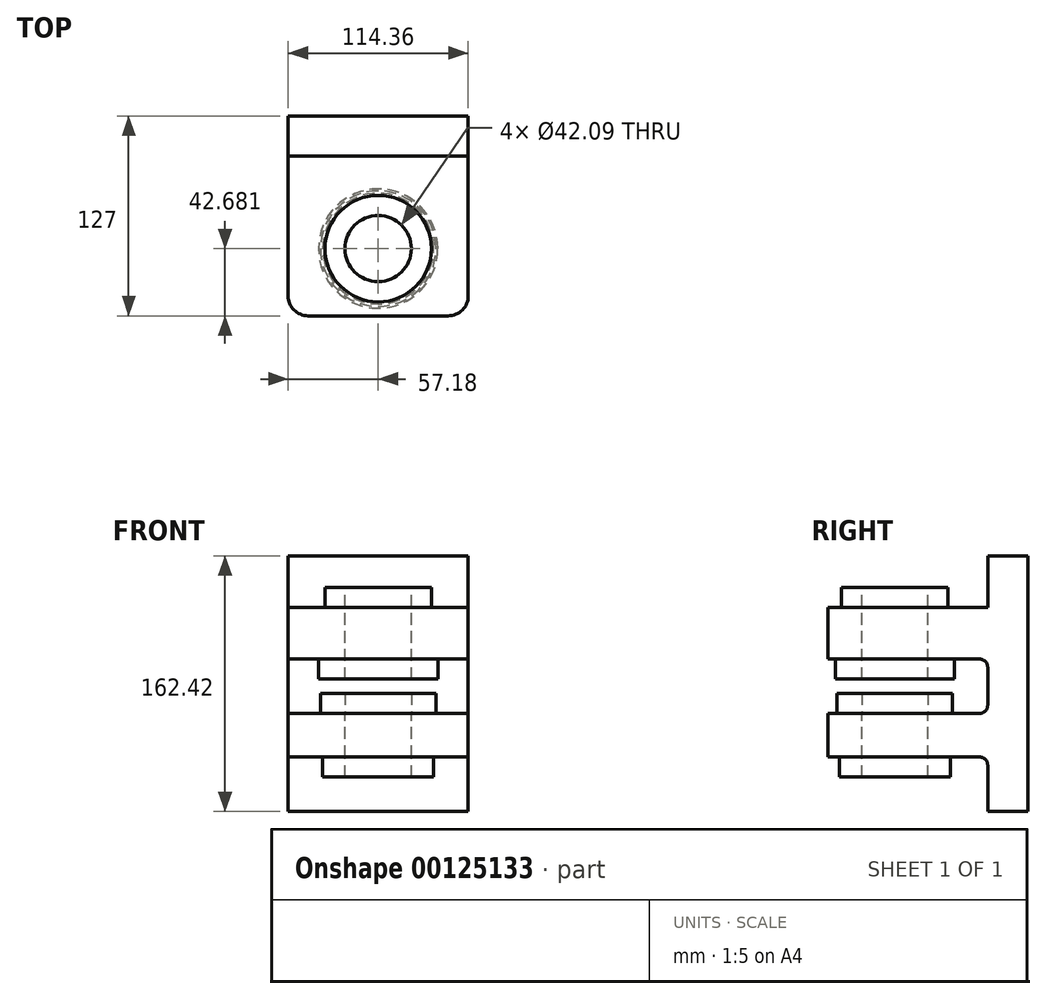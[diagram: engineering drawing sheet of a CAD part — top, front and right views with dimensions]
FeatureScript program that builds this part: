
annotation { "Feature Type Name" : "Feature", "Feature Type Description" : "" }
export const myFeature = defineFeature(function(context is Context, id is Id, definition is map)
    precondition{}
    {
        {
            var Q0;
            Q0=qCreatedBy(makeId("Front.planeOp"),FACE);
            var sketch = newSketch(context, id + "F0", { "sketchPlane" : qUnion([Q0])});
            skLineSegment(sketch, "E0.bottom", {"start": v(-57.18, 81.21) * mm, "end": v(57.18, 81.21) * mm});
            skLineSegment(sketch, "E0.top", {"start": v(-57.18, -81.21) * mm, "end": v(57.18, -81.21) * mm});
            skLineSegment(sketch, "E0.left", {"start": v(-57.18, 81.21) * mm, "end": v(-57.18, -81.21) * mm});
            skLineSegment(sketch, "E0.right", {"start": v(57.18, 81.21) * mm, "end": v(57.18, -81.21) * mm});
            skPoint(sketch, "E0.middle", {"position": v(0, 0) * mm});
            skSolve(sketch);
        }
        {
            var Q0;
            Q0=makeQuery(id+"F0.imprint","IMPRINT",FACE,{"disambiguationData":[TD([[makeQuery(id+"F0.imprint","IMPRINT",EDGE,{"derivedFrom":sQuery(id+"F0.wireOp",EDGE,"E0.bottom")}),-1.0]])]});
            extrude(context, id + "F1", {"entities" : qUnion([Q0]), "depth" : 25.4 * mm});
        }
        {
            var Q0;
            Q0=makeQuery(id+"F1.opExtrude","CAP_FACE",FACE,{"disambiguationData":[OSD([sQuery(id+"F0.wireOp",EDGE,"E0.bottom"),sQuery(id+"F0.wireOp",EDGE,"E0.top"),sQuery(id+"F0.wireOp",EDGE,"E0.left"),sQuery(id+"F0.wireOp",EDGE,"E0.right")])],"isStart":false});
            var sketch = newSketch(context, id + "F2", { "sketchPlane" : qUnion([Q0])});
            skLineSegment(sketch, "E1.bottom", {"start": v(57.18, 48.51) * mm, "end": v(-57.18, 48.51) * mm});
            skLineSegment(sketch, "E1.top", {"start": v(57.18, 15.68) * mm, "end": v(-57.18, 15.68) * mm});
            skLineSegment(sketch, "E1.left", {"start": v(57.18, 48.51) * mm, "end": v(57.18, 15.68) * mm});
            skLineSegment(sketch, "E1.right", {"start": v(-57.18, 48.51) * mm, "end": v(-57.18, 15.68) * mm});
            skLineSegment(sketch, "E2.bottom", {"start": v(57.18, -18.79) * mm, "end": v(-57.18, -18.79) * mm});
            skLineSegment(sketch, "E2.top", {"start": v(57.18, -46.54) * mm, "end": v(-57.18, -46.54) * mm});
            skLineSegment(sketch, "E2.left", {"start": v(57.18, -18.79) * mm, "end": v(57.18, -46.54) * mm});
            skLineSegment(sketch, "E2.right", {"start": v(-57.18, -18.79) * mm, "end": v(-57.18, -46.54) * mm});
            skSolve(sketch);
        }
        {
            var Q0;
            Q0=makeQuery(id+"F2.imprint","IMPRINT",FACE,{"disambiguationData":[TD([[makeQuery(id+"F2.imprint","IMPRINT",EDGE,{"derivedFrom":sQuery(id+"F2.wireOp",EDGE,"E1.bottom")}),1.0]])]});
            var Q1;
            Q1=makeQuery(id+"F2.imprint","IMPRINT",FACE,{"disambiguationData":[TD([[makeQuery(id+"F2.imprint","IMPRINT",EDGE,{"derivedFrom":sQuery(id+"F2.wireOp",EDGE,"E2.bottom")}),1.0]])]});
            extrude(context, id + "F3", {"entities" : qUnion([Q0, Q1]), "operationType" : NewBodyOperationType.ADD, "depth" : 101.6 * mm});
        }
        {
            var Q0;
            Q0=makeQuery(id+"F3.opExtrude","SWEPT_FACE",FACE,{"disambiguationData":[OSD([sQuery(id+"F2.wireOp",EDGE,"E1.bottom")])]});
            var sketch = newSketch(context, id + "F4", { "sketchPlane" : qUnion([Q0])});
            skCircle(sketch, "E3", {"center": v(0, -84.32) * mm, "radius": 21.04 * mm});
            skSolve(sketch);
        }
        {
            var Q0;
            Q0=makeQuery(id+"F4.imprint","IMPRINT",FACE,{"disambiguationData":[TD([[makeQuery(id+"F4.imprint","IMPRINT",EDGE,{"derivedFrom":sQuery(id+"F4.wireOp",EDGE,"E3")}),1.0]])]});
            var Q1;
            Q1=makeQuery(id+"F3.opExtrude","SWEPT_FACE",FACE,{"disambiguationData":[OSD([sQuery(id+"F2.wireOp",EDGE,"E2.top")])]});
            extrude(context, id + "F5", {"entities" : qUnion([Q0, Q1]), "operationType" : NewBodyOperationType.REMOVE, "oppositeDirection" : true, "depth" : 228.6 * mm});
        }
        {
            var Q0;
            Q0=makeQuery(id+"F3.opExtrude","SWEPT_FACE",FACE,{"disambiguationData":[OSD([sQuery(id+"F2.wireOp",EDGE,"E1.bottom")])]});
            var sketch = newSketch(context, id + "F6", { "sketchPlane" : qUnion([Q0])});
            skCircle(sketch, "E4", {"center": v(0, -84.32) * mm, "radius": 33.82 * mm});
            skSolve(sketch);
        }
        {
            var Q0;
            Q0=makeQuery(id+"F3.opExtrude","SWEPT_FACE",FACE,{"disambiguationData":[OSD([sQuery(id+"F2.wireOp",EDGE,"E1.top")])]});
            var sketch = newSketch(context, id + "F7", { "sketchPlane" : qUnion([Q0])});
            skCircle(sketch, "E5", {"center": v(0, 84.32) * mm, "radius": 37.87 * mm});
            skSolve(sketch);
        }
        {
            var Q0;
            Q0=makeQuery(id+"F3.opExtrude","SWEPT_FACE",FACE,{"disambiguationData":[OSD([sQuery(id+"F2.wireOp",EDGE,"E2.bottom")])]});
            var sketch = newSketch(context, id + "F8", { "sketchPlane" : qUnion([Q0])});
            skCircle(sketch, "E6", {"center": v(0, -84.32) * mm, "radius": 36.66 * mm});
            skSolve(sketch);
        }
        {
            var Q0;
            Q0=makeQuery(id+"F3.opExtrude","SWEPT_FACE",FACE,{"disambiguationData":[OSD([sQuery(id+"F2.wireOp",EDGE,"E2.top")])]});
            var sketch = newSketch(context, id + "F9", { "sketchPlane" : qUnion([Q0])});
            skCircle(sketch, "E7", {"center": v(0, 84.32) * mm, "radius": 35.21 * mm});
            skSolve(sketch);
        }
        {
            var Q0;
            Q0=makeQuery(id+"F6.imprint","IMPRINT",FACE,{"disambiguationData":[TD([[makeQuery(id+"F6.imprint","IMPRINT",EDGE,{"derivedFrom":sQuery(id+"F6.wireOp",EDGE,"E4")}),1.0]])]});
            extrude(context, id + "F10", {"entities" : qUnion([Q0]), "operationType" : NewBodyOperationType.ADD, "depth" : 12.7 * mm});
        }
        {
            var Q0;
            Q0=makeQuery(id+"F9.imprint","IMPRINT",FACE,{"disambiguationData":[TD([[makeQuery(id+"F9.imprint","IMPRINT",EDGE,{"derivedFrom":sQuery(id+"F9.wireOp",EDGE,"E7")}),1.0]])]});
            var Q1;
            Q1=sQuery(id+"F9.wireOp",EDGE,"E7");
            extrude(context, id + "F11", {"entities" : qUnion([Q0]), "surfaceEntities" : qUnion([Q1]), "depth" : 12.7 * mm});
        }
        {
            var Q0;
            Q0=makeQuery(id+"F3.opExtrude","CAP_EDGE",EDGE,{"disambiguationData":[OSD([sQuery(id+"F2.wireOp",EDGE,"E1.bottom")])],"isStart":true});
            var Q1;
            Q1=makeQuery(id+"F3.opExtrude","CAP_EDGE",EDGE,{"disambiguationData":[OSD([sQuery(id+"F2.wireOp",EDGE,"E1.top")])],"isStart":true});
            var Q2;
            Q2=makeQuery(id+"F3.opExtrude","CAP_EDGE",EDGE,{"disambiguationData":[OSD([sQuery(id+"F2.wireOp",EDGE,"E2.bottom")])],"isStart":true});
            var Q3;
            Q3=makeQuery(id+"F3.opExtrude","CAP_EDGE",EDGE,{"disambiguationData":[OSD([sQuery(id+"F2.wireOp",EDGE,"E2.top")])],"isStart":true});
            fillet(context, id + "F12", {"entities" : qUnion([Q0, Q1, Q2, Q3]), "radius" : 5.08 * mm, "tangentPropagation" : true, "allowEdgeOverflow" : false});
        }
        {
            var Q0;
            Q0=makeQuery(id+"F7.imprint","IMPRINT",FACE,{"disambiguationData":[TD([[makeQuery(id+"F7.imprint","IMPRINT",EDGE,{"derivedFrom":sQuery(id+"F7.wireOp",EDGE,"E5")}),1.0]])]});
            extrude(context, id + "F13", {"entities" : qUnion([Q0]), "operationType" : NewBodyOperationType.ADD, "depth" : 12.7 * mm});
        }
        {
            var Q0;
            Q0=makeQuery(id+"F8.imprint","IMPRINT",FACE,{"disambiguationData":[TD([[makeQuery(id+"F8.imprint","IMPRINT",EDGE,{"derivedFrom":sQuery(id+"F8.wireOp",EDGE,"E6")}),1.0]])]});
            var Q1;
            Q1=sQuery(id+"F8.wireOp",EDGE,"E6");
            extrude(context, id + "F14", {"entities" : qUnion([Q0]), "surfaceEntities" : qUnion([Q1]), "depth" : 12.7 * mm});
        }
        {
            var Q0;
            Q0=makeQuery(id+"F3.opExtrude","CAP_EDGE",EDGE,{"disambiguationData":[OSD([sQuery(id+"F2.wireOp",EDGE,"E2.left")])],"isStart":false});
            var Q1;
            Q1=makeQuery(id+"F3.opExtrude","CAP_EDGE",EDGE,{"disambiguationData":[OSD([sQuery(id+"F2.wireOp",EDGE,"E1.left")])],"isStart":false});
            var Q2;
            Q2=makeQuery(id+"F3.opExtrude","CAP_EDGE",EDGE,{"disambiguationData":[OSD([sQuery(id+"F2.wireOp",EDGE,"E2.right")])],"isStart":false});
            var Q3;
            Q3=makeQuery(id+"F3.opExtrude","CAP_EDGE",EDGE,{"disambiguationData":[OSD([sQuery(id+"F2.wireOp",EDGE,"E1.right")])],"isStart":false});
            fillet(context, id + "F15", {"entities" : qUnion([Q0, Q1, Q2, Q3]), "radius" : 12.7 * mm, "tangentPropagation" : true, "allowEdgeOverflow" : false});
        }
    });
